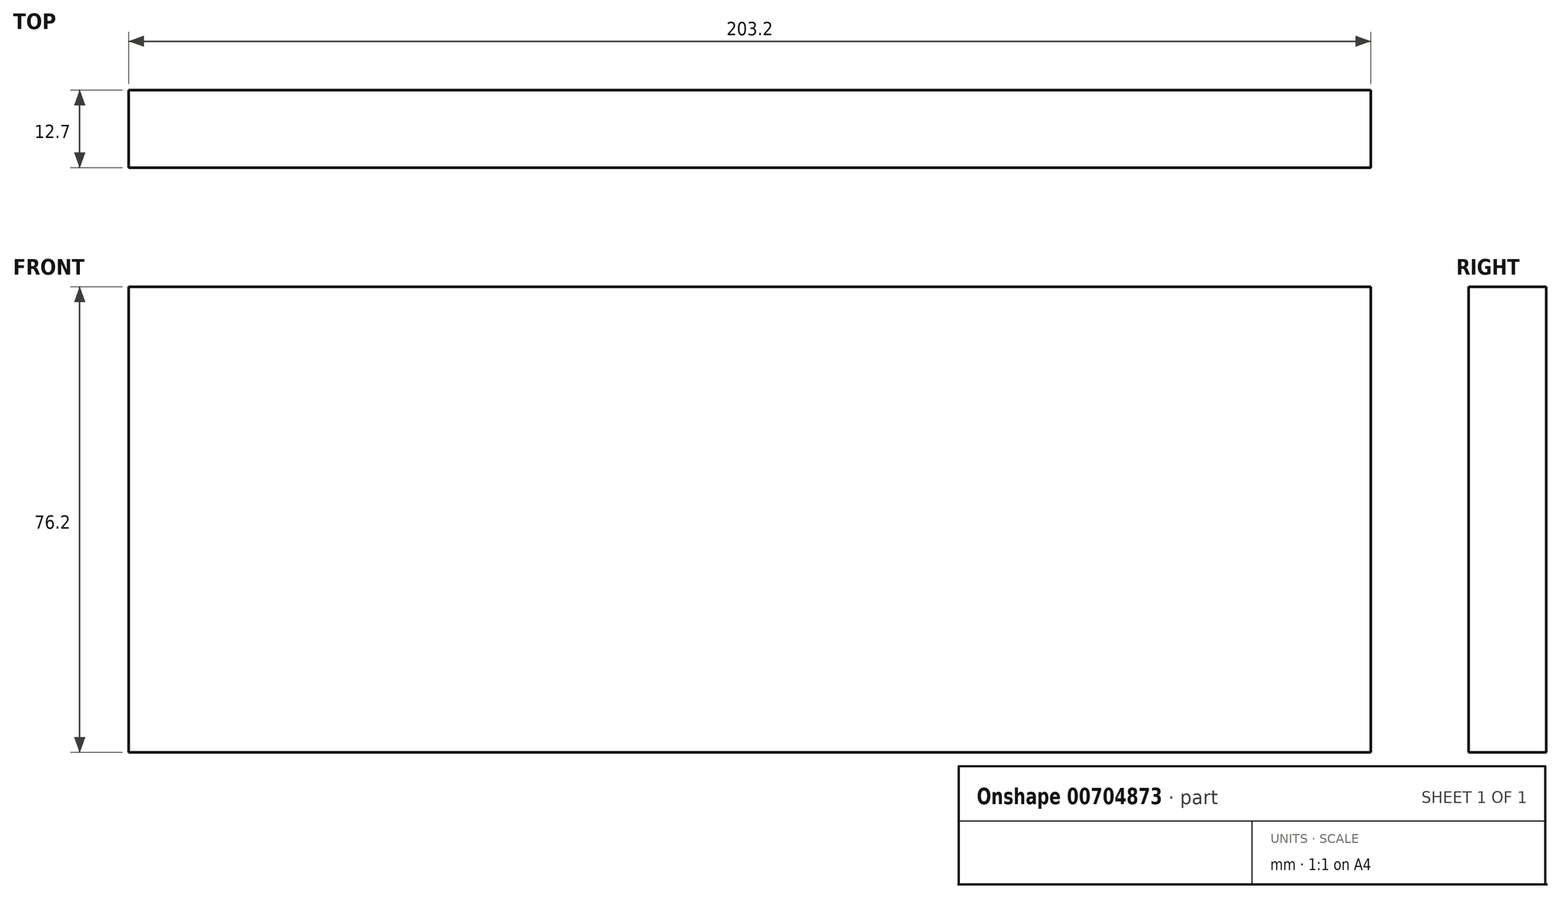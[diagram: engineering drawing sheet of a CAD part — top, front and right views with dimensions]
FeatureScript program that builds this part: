
annotation { "Feature Type Name" : "Feature", "Feature Type Description" : "" }
export const myFeature = defineFeature(function(context is Context, id is Id, definition is map)
    precondition{}
    {
        {
            var Q0;
            Q0=qCreatedBy(makeId("Front.planeOp"),FACE);
            var sketch = newSketch(context, id + "F0", { "sketchPlane" : qUnion([Q0])});
            skLineSegment(sketch, "E0.bottom", {"start": v(-53.09, 42.46) * mm, "end": v(150.11, 42.46) * mm});
            skLineSegment(sketch, "E0.top", {"start": v(-53.09, -33.74) * mm, "end": v(150.11, -33.74) * mm});
            skLineSegment(sketch, "E0.left", {"start": v(-53.09, 42.46) * mm, "end": v(-53.09, -33.74) * mm});
            skLineSegment(sketch, "E0.right", {"start": v(150.11, 42.46) * mm, "end": v(150.11, -33.74) * mm});
            skSolve(sketch);
        }
        {
            var Q0;
            Q0=makeQuery(id+"F0.imprint","IMPRINT",FACE,{"disambiguationData":[TD([[makeQuery(id+"F0.imprint","IMPRINT",EDGE,{"derivedFrom":sQuery(id+"F0.wireOp",EDGE,"E0.bottom")}),-1.0]])]});
            extrude(context, id + "F1", {"entities" : qUnion([Q0]), "depth" : 12.7 * mm, "offsetDistance" : 25.4 * mm});
        }
    });
